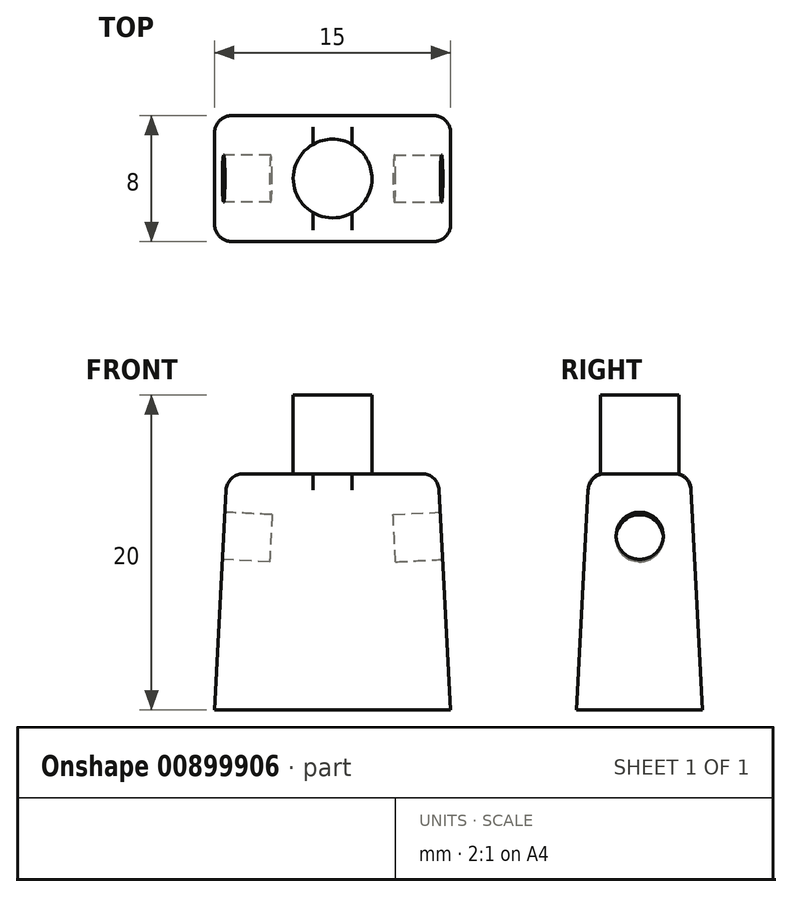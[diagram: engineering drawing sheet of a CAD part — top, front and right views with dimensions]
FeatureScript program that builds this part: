
annotation { "Feature Type Name" : "Feature", "Feature Type Description" : "" }
export const myFeature = defineFeature(function(context is Context, id is Id, definition is map)
    precondition{}
    {
        {
            var Q0;
            Q0=qCreatedBy(makeId("Top.planeOp"),FACE);
            var sketch = newSketch(context, id + "F0", { "sketchPlane" : qUnion([Q0])});
            skLineSegment(sketch, "E0.bottom", {"start": v(7.5, -4) * mm, "end": v(-7.5, -4) * mm});
            skLineSegment(sketch, "E0.top", {"start": v(7.5, 4) * mm, "end": v(-7.5, 4) * mm});
            skLineSegment(sketch, "E0.left", {"start": v(7.5, -4) * mm, "end": v(7.5, 4) * mm});
            skLineSegment(sketch, "E0.right", {"start": v(-7.5, -4) * mm, "end": v(-7.5, 4) * mm});
            skPoint(sketch, "E0.middle", {"position": v(0, 0) * mm});
            skSolve(sketch);
        }
        {
            var Q0;
            Q0 = qSketchRegion(id + "F0", true);
            extrude(context, id + "F1", {"entities" : qUnion([Q0]), "depth" : 15 * mm, "offsetDistance" : 25.4 * mm, "hasDraft" : true, "draftAngle" : 3 * degree, "draftPullDirection" : true});
        }
        {
            var Q0;
            Q0=makeQuery(id+"F1.opExtrude","CAP_FACE",FACE,{"disambiguationData":[OSD([sQuery(id+"F0.wireOp",EDGE,"E0.bottom"),sQuery(id+"F0.wireOp",EDGE,"E0.top"),sQuery(id+"F0.wireOp",EDGE,"E0.left"),sQuery(id+"F0.wireOp",EDGE,"E0.right")])],"isStart":false});
            var sketch = newSketch(context, id + "F2", { "sketchPlane" : qUnion([Q0])});
            skCircle(sketch, "E1", {"center": v(0, 0) * mm, "radius": 2.5 * mm});
            skSolve(sketch);
        }
        {
            var Q0;
            Q0 = qSketchRegion(id + "F2", true);
            extrude(context, id + "F3", {"entities" : qUnion([Q0]), "operationType" : NewBodyOperationType.ADD, "depth" : 5 * mm, "offsetDistance" : 25.4 * mm});
        }
        {
            var Q0;
            Q0=makeQuery(id+"F1.opExtrude","SWEPT_EDGE",EDGE,{"disambiguationData":[OSD([sQuery(id+"F0.wireOp",EDGE,"E0.top"),sQuery(id+"F0.wireOp",EDGE,"E0.left")])]});
            var Q1;
            Q1=makeQuery(id+"F1.opExtrude","SWEPT_EDGE",EDGE,{"disambiguationData":[OSD([sQuery(id+"F0.wireOp",EDGE,"E0.top"),sQuery(id+"F0.wireOp",EDGE,"E0.right")])]});
            var Q2;
            Q2=makeQuery(id+"F1.opExtrude","CAP_EDGE",EDGE,{"disambiguationData":[OSD([sQuery(id+"F0.wireOp",EDGE,"E0.top")])],"isStart":false});
            var Q3;
            Q3=makeQuery(id+"F1.opExtrude","CAP_EDGE",EDGE,{"disambiguationData":[OSD([sQuery(id+"F0.wireOp",EDGE,"E0.right")])],"isStart":false});
            var Q4;
            Q4=makeQuery(id+"F1.opExtrude","CAP_EDGE",EDGE,{"disambiguationData":[OSD([sQuery(id+"F0.wireOp",EDGE,"E0.left")])],"isStart":false});
            var Q5;
            Q5=makeQuery(id+"F1.opExtrude","CAP_EDGE",EDGE,{"disambiguationData":[OSD([sQuery(id+"F0.wireOp",EDGE,"E0.bottom")])],"isStart":false});
            var Q6;
            Q6=makeQuery(id+"F1.opExtrude","SWEPT_EDGE",EDGE,{"disambiguationData":[OSD([sQuery(id+"F0.wireOp",EDGE,"E0.bottom"),sQuery(id+"F0.wireOp",EDGE,"E0.left")])]});
            var Q7;
            Q7=makeQuery(id+"F1.opExtrude","SWEPT_EDGE",EDGE,{"disambiguationData":[OSD([sQuery(id+"F0.wireOp",EDGE,"E0.bottom"),sQuery(id+"F0.wireOp",EDGE,"E0.right")])]});
            fillet(context, id + "F4", {"entities" : qUnion([Q0, Q1, Q2, Q3, Q4, Q5, Q6, Q7]), "radius" : 1.1 * mm, "tangentPropagation" : true, "allowEdgeOverflow" : false});
        }
        {
            var Q0;
            Q0=makeQuery(id+"F1.opExtrude","SWEPT_FACE",FACE,{"disambiguationData":[OSD([sQuery(id+"F0.wireOp",EDGE,"E0.right")])]});
            var sketch = newSketch(context, id + "F5", { "sketchPlane" : qUnion([Q0])});
            skCircle(sketch, "E2", {"center": v(0, 10.68) * mm, "radius": 1.5 * mm});
            skSolve(sketch);
        }
        {
            var Q0;
            Q0=makeQuery(id+"F5.imprint","IMPRINT",FACE,{"disambiguationData":[TD([[makeQuery(id+"F5.imprint","IMPRINT",EDGE,{"derivedFrom":sQuery(id+"F5.wireOp",EDGE,"E2")}),1.0]])]});
            extrude(context, id + "F6", {"entities" : qUnion([Q0]), "operationType" : NewBodyOperationType.REMOVE, "oppositeDirection" : true, "depth" : 3 * mm, "offsetDistance" : 25.4 * mm});
        }
        {
            var Q0;
            Q0=makeQuery(id+"F1.opExtrude","SWEPT_FACE",FACE,{"disambiguationData":[OSD([sQuery(id+"F0.wireOp",EDGE,"E0.left")])]});
            var sketch = newSketch(context, id + "F7", { "sketchPlane" : qUnion([Q0])});
            skCircle(sketch, "E3", {"center": v(0, 10.68) * mm, "radius": 1.5 * mm});
            skSolve(sketch);
        }
        {
            var Q0;
            Q0=makeQuery(id+"F7.imprint","IMPRINT",FACE,{"disambiguationData":[TD([[makeQuery(id+"F7.imprint","IMPRINT",EDGE,{"derivedFrom":sQuery(id+"F7.wireOp",EDGE,"E3")}),1.0]])]});
            extrude(context, id + "F8", {"entities" : qUnion([Q0]), "operationType" : NewBodyOperationType.REMOVE, "oppositeDirection" : true, "depth" : 3 * mm, "offsetDistance" : 25.4 * mm});
        }
    });
